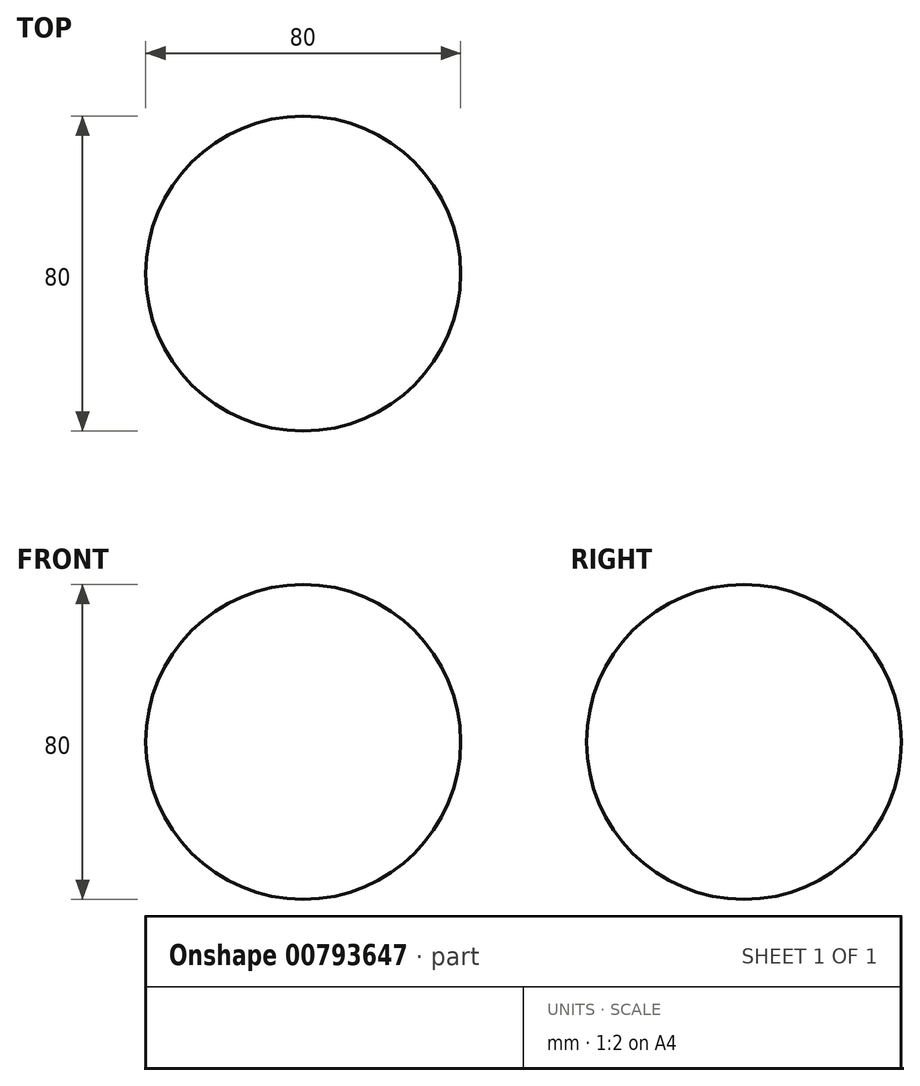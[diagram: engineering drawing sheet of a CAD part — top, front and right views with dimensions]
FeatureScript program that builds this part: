
annotation { "Feature Type Name" : "Feature", "Feature Type Description" : "" }
export const myFeature = defineFeature(function(context is Context, id is Id, definition is map)
    precondition{}
    {
        {
            var Q0;
            Q0=qCreatedBy(makeId("Front.planeOp"),FACE);
            var sketch = newSketch(context, id + "F0", { "sketchPlane" : qUnion([Q0])});
            skLineSegment(sketch, "E0.bottom", {"start": v(40, -40) * mm, "end": v(-40, -40) * mm});
            skLineSegment(sketch, "E0.top", {"start": v(40, 40) * mm, "end": v(-40, 40) * mm});
            skLineSegment(sketch, "E0.left", {"start": v(40, -40) * mm, "end": v(40, 40) * mm});
            skLineSegment(sketch, "E0.right", {"start": v(-40, -40) * mm, "end": v(-40, 40) * mm});
            skPoint(sketch, "E0.middle", {"position": v(0, 0) * mm});
            skCircle(sketch, "E1", {"center": v(0, 0) * mm, "radius": 40 * mm});
            skSolve(sketch);
        }
        {
            var Q0;
            Q0=qCreatedBy(makeId("Front.planeOp"),FACE);
            cPlane(context, id + "F1", {"entities" : qUnion([Q0]), "cplaneType" : CPlaneType.OFFSET, "offset" : 0 * mm, "width" : 150 * mm, "height" : 150 * mm});
        }
        {
            var Q0;
            Q0=qCreatedBy(id+"F1.planeOp",FACE);
            var sketch = newSketch(context, id + "F2", { "sketchPlane" : qUnion([Q0])});
            skArc(sketch, "E2.0", {"start": v(0, -40) * mm, "mid": v(40, 0) * mm, "end": v(0, 40) * mm});
            skLineSegment(sketch, "E3", {"start": v(0, 40) * mm, "end": v(0, -40) * mm});
            skLineSegment(sketch, "E4", {"start": v(0, 48.14) * mm, "end": v(0, -45.03) * mm, "construction": true});
            skSolve(sketch);
        }
        {
            var Q0;
            Q0 = qSketchRegion(id + "F2", true);
            var Q1;
            Q1=sQuery(id+"F2.wireOp",EDGE,"E4");
            revolve(context, id + "F3", {"surfaceOperationType" : NewSurfaceOperationType.NEW, "entities" : qUnion([Q0]), "axis" : qUnion([Q1]), "revolveType" : RevolveType.FULL});
        }
    });
